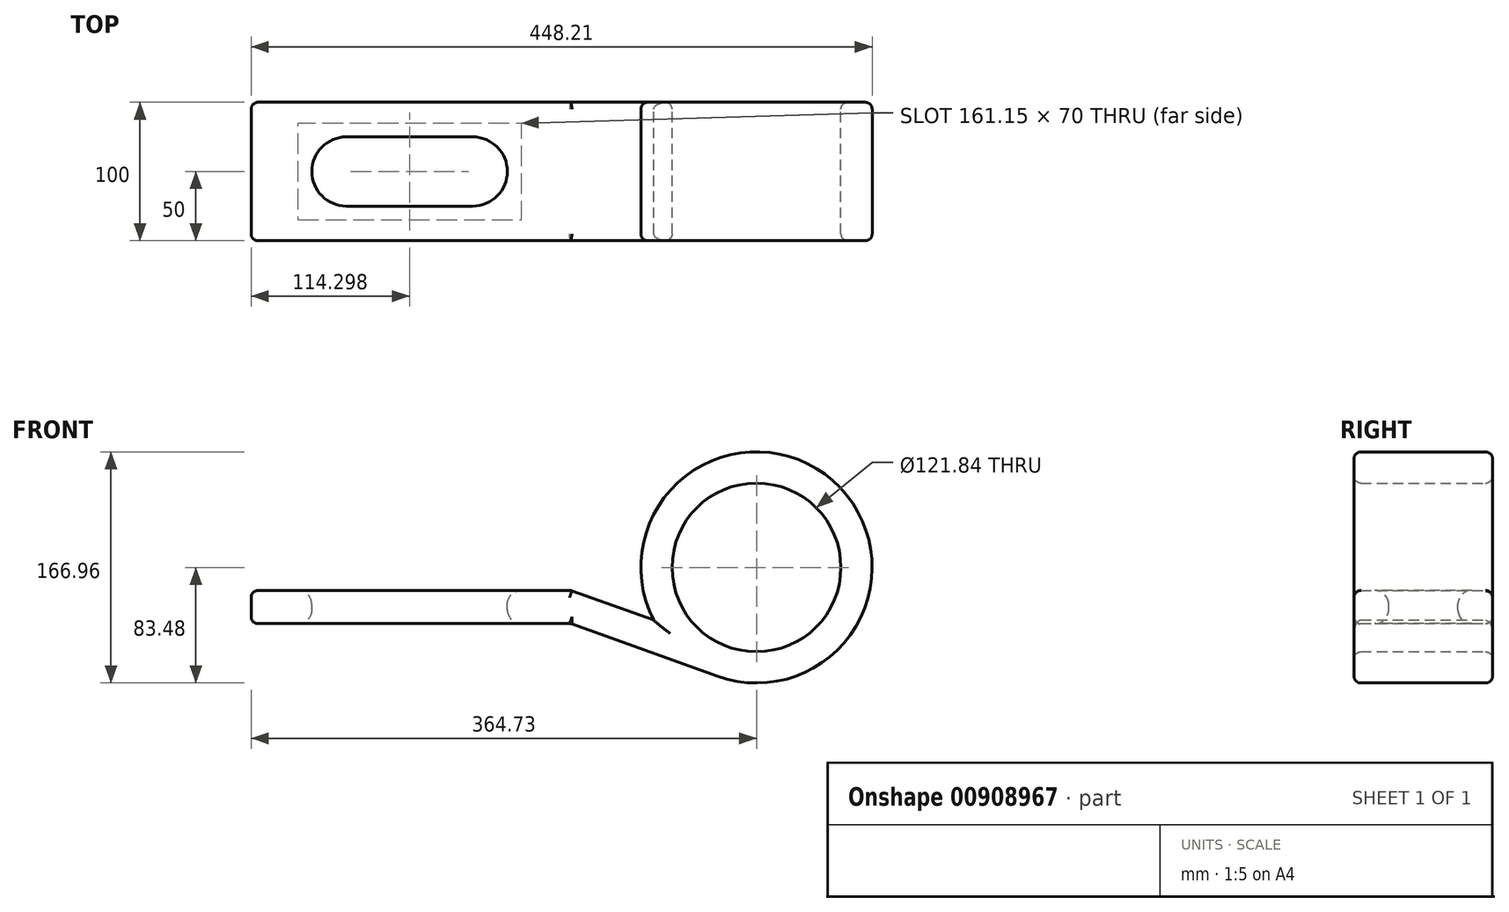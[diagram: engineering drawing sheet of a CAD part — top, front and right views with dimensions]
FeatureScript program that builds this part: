
annotation { "Feature Type Name" : "Feature", "Feature Type Description" : "" }
export const myFeature = defineFeature(function(context is Context, id is Id, definition is map)
    precondition{}
    {
        {
            var Q0;
            Q0=qCreatedBy(makeId("Front.planeOp"),FACE);
            var sketch = newSketch(context, id + "F0", { "sketchPlane" : qUnion([Q0])});
            skLineSegment(sketch, "E0.bottom", {"start": v(-96.99, -16.6) * mm, "end": v(133.68, -16.6) * mm});
            skLineSegment(sketch, "E0.top", {"start": v(-96.99, -40.57) * mm, "end": v(133.68, -40.57) * mm});
            skLineSegment(sketch, "E0.left", {"start": v(-96.99, -16.6) * mm, "end": v(-96.99, -40.57) * mm});
            skLineSegment(sketch, "E0.right", {"start": v(133.68, -16.6) * mm, "end": v(133.68, -40.57) * mm});
            skCircle(sketch, "E1", {"center": v(267.74, 0) * mm, "radius": 60.92 * mm});
            skLineSegment(sketch, "E2", {"start": v(133.68, -16.6) * mm, "end": v(193.44, -38.05) * mm});
            skLineSegment(sketch, "E3", {"start": v(133.68, -40.57) * mm, "end": v(239.53, -78.57) * mm});
            skArc(sketch, "E4", {"start": v(239.53, -78.57) * mm, "mid": v(322.85, 62.7) * mm, "end": v(193.44, -38.05) * mm});
            skSolve(sketch);
        }
        {
            var Q0;
            Q0 = qSketchRegion(id + "F0", true);
            extrude(context, id + "F1", {"entities" : qUnion([Q0]), "depth" : 100 * mm, "offsetDistance" : 25 * mm});
        }
        {
            var Q0;
            Q0=makeQuery(id+"F1.opExtrude","CAP_EDGE",EDGE,{"disambiguationData":[OSD([sQuery(id+"F0.wireOp",EDGE,"E3")])],"isStart":true});
            var Q1;
            Q1=makeQuery(id+"F1.opExtrude","CAP_EDGE",EDGE,{"disambiguationData":[OSD([sQuery(id+"F0.wireOp",EDGE,"E0.top")])],"isStart":true});
            var Q2;
            Q2=makeQuery(id+"F1.opExtrude","CAP_EDGE",EDGE,{"disambiguationData":[OSD([sQuery(id+"F0.wireOp",EDGE,"E0.bottom")])],"isStart":true});
            var Q3;
            Q3=makeQuery(id+"F1.opExtrude","CAP_EDGE",EDGE,{"disambiguationData":[OSD([sQuery(id+"F0.wireOp",EDGE,"E2")])],"isStart":true});
            var Q4;
            Q4=makeQuery(id+"F1.opExtrude","SWEPT_EDGE",EDGE,{"disambiguationData":[OSD([sQuery(id+"F0.wireOp",EDGE,"E0.bottom"),sQuery(id+"F0.wireOp",EDGE,"E0.left")])]});
            var Q5;
            Q5=makeQuery(id+"F1.opExtrude","CAP_EDGE",EDGE,{"disambiguationData":[OSD([sQuery(id+"F0.wireOp",EDGE,"E0.left")])],"isStart":true});
            var Q6;
            Q6=makeQuery(id+"F1.opExtrude","CAP_EDGE",EDGE,{"disambiguationData":[OSD([sQuery(id+"F0.wireOp",EDGE,"E1")])],"isStart":false});
            var Q7;
            Q7=makeQuery(id+"F1.opExtrude","CAP_EDGE",EDGE,{"disambiguationData":[OSD([sQuery(id+"F0.wireOp",EDGE,"E4")])],"isStart":false});
            var Q8;
            Q8=makeQuery(id+"F1.opExtrude","CAP_FACE",FACE,{"disambiguationData":[OSD([sQuery(id+"F0.wireOp",EDGE,"E0.bottom"),sQuery(id+"F0.wireOp",EDGE,"E0.top"),sQuery(id+"F0.wireOp",EDGE,"E0.left"),sQuery(id+"F0.wireOp",EDGE,"E1"),sQuery(id+"F0.wireOp",EDGE,"E2"),sQuery(id+"F0.wireOp",EDGE,"E3"),sQuery(id+"F0.wireOp",EDGE,"E4")])],"isStart":false});
            fillet(context, id + "F2", {"entities" : qUnion([Q0, Q1, Q2, Q3, Q4, Q5, Q6, Q7, Q8]), "radius" : 5 * mm, "tangentPropagation" : true, "allowEdgeOverflow" : false});
        }
        {
            var Q0;
            Q0=makeQuery(id+"F1.opExtrude","CAP_EDGE",EDGE,{"disambiguationData":[OSD([sQuery(id+"F0.wireOp",EDGE,"E1")])],"isStart":true});
            fillet(context, id + "F3", {"entities" : qUnion([Q0]), "radius" : 5 * mm, "tangentPropagation" : true, "allowEdgeOverflow" : false});
        }
        {
            var Q0;
            Q0=qCreatedBy(makeId("Top.planeOp"),FACE);
            var sketch = newSketch(context, id + "F4", { "sketchPlane" : qUnion([Q0])});
            skCircle(sketch, "E5", {"center": v(-28.27, -50) * mm, "radius": 25 * mm});
            skCircle(sketch, "E6", {"center": v(62.88, -50) * mm, "radius": 25 * mm});
            skLineSegment(sketch, "E7", {"start": v(-28.27, -25) * mm, "end": v(62.88, -25) * mm});
            skLineSegment(sketch, "E8", {"start": v(-28.27, -75) * mm, "end": v(62.88, -75) * mm});
            skSolve(sketch);
        }
        {
            var Q0;
            Q0 = qSketchRegion(id + "F4", true);
            extrude(context, id + "F5", {"entities" : qUnion([Q0]), "operationType" : NewBodyOperationType.REMOVE, "oppositeDirection" : true, "depth" : 126.8 * mm, "offsetDistance" : 25 * mm});
        }
        {
            var Q0;
            Q0=makeQuery(id+"F5.boolean.opBoolean","INTERSECT",EDGE,{"derivedFrom":[makeQuery(id+"F1.opExtrude","SWEPT_FACE",FACE,{"disambiguationData":[OSD([sQuery(id+"F0.wireOp",EDGE,"E0.top")])]}),makeQuery(id+"F5.opExtrude","SWEPT_FACE",FACE,{"disambiguationData":[OSD([sQuery(id+"F4.wireOp",EDGE,"E8")])]})]});
            var Q1;
            Q1=makeQuery(id+"F5.boolean.opBoolean","INTERSECT",EDGE,{"derivedFrom":[makeQuery(id+"F1.opExtrude","SWEPT_FACE",FACE,{"disambiguationData":[OSD([sQuery(id+"F0.wireOp",EDGE,"E0.bottom")])]}),makeQuery(id+"F5.opExtrude","SWEPT_FACE",FACE,{"disambiguationData":[OSD([sQuery(id+"F4.wireOp",EDGE,"E7")])]})]});
            fillet(context, id + "F6", {"entities" : qUnion([Q0, Q1]), "radius" : 10 * mm, "tangentPropagation" : true, "allowEdgeOverflow" : false});
        }
        {
            var Q0;
            Q0=makeQuery(id+"F1.opExtrude","SWEPT_EDGE",EDGE,{"disambiguationData":[OSD([sQuery(id+"F0.wireOp",EDGE,"E0.top"),sQuery(id+"F0.wireOp",EDGE,"E0.left")])]});
            fillet(context, id + "F7", {"entities" : qUnion([Q0]), "radius" : 5 * mm, "tangentPropagation" : true, "allowEdgeOverflow" : false});
        }
        {
            var Q0;
            Q0=makeQuery(id+"F1.opExtrude","SWEPT_EDGE",EDGE,{"disambiguationData":[OSD([sQuery(id+"F0.wireOp",EDGE,"E0.top"),sQuery(id+"F0.wireOp",EDGE,"E0.right"),sQuery(id+"F0.wireOp",EDGE,"E3")])]});
            var Q1;
            Q1=makeQuery(id+"F1.opExtrude","SWEPT_EDGE",EDGE,{"disambiguationData":[OSD([sQuery(id+"F0.wireOp",EDGE,"E0.bottom"),sQuery(id+"F0.wireOp",EDGE,"E0.right"),sQuery(id+"F0.wireOp",EDGE,"E2")])]});
            fillet(context, id + "F8", {"entities" : qUnion([Q0, Q1]), "radius" : 5 * mm, "tangentPropagation" : true, "allowEdgeOverflow" : false});
        }
    });
